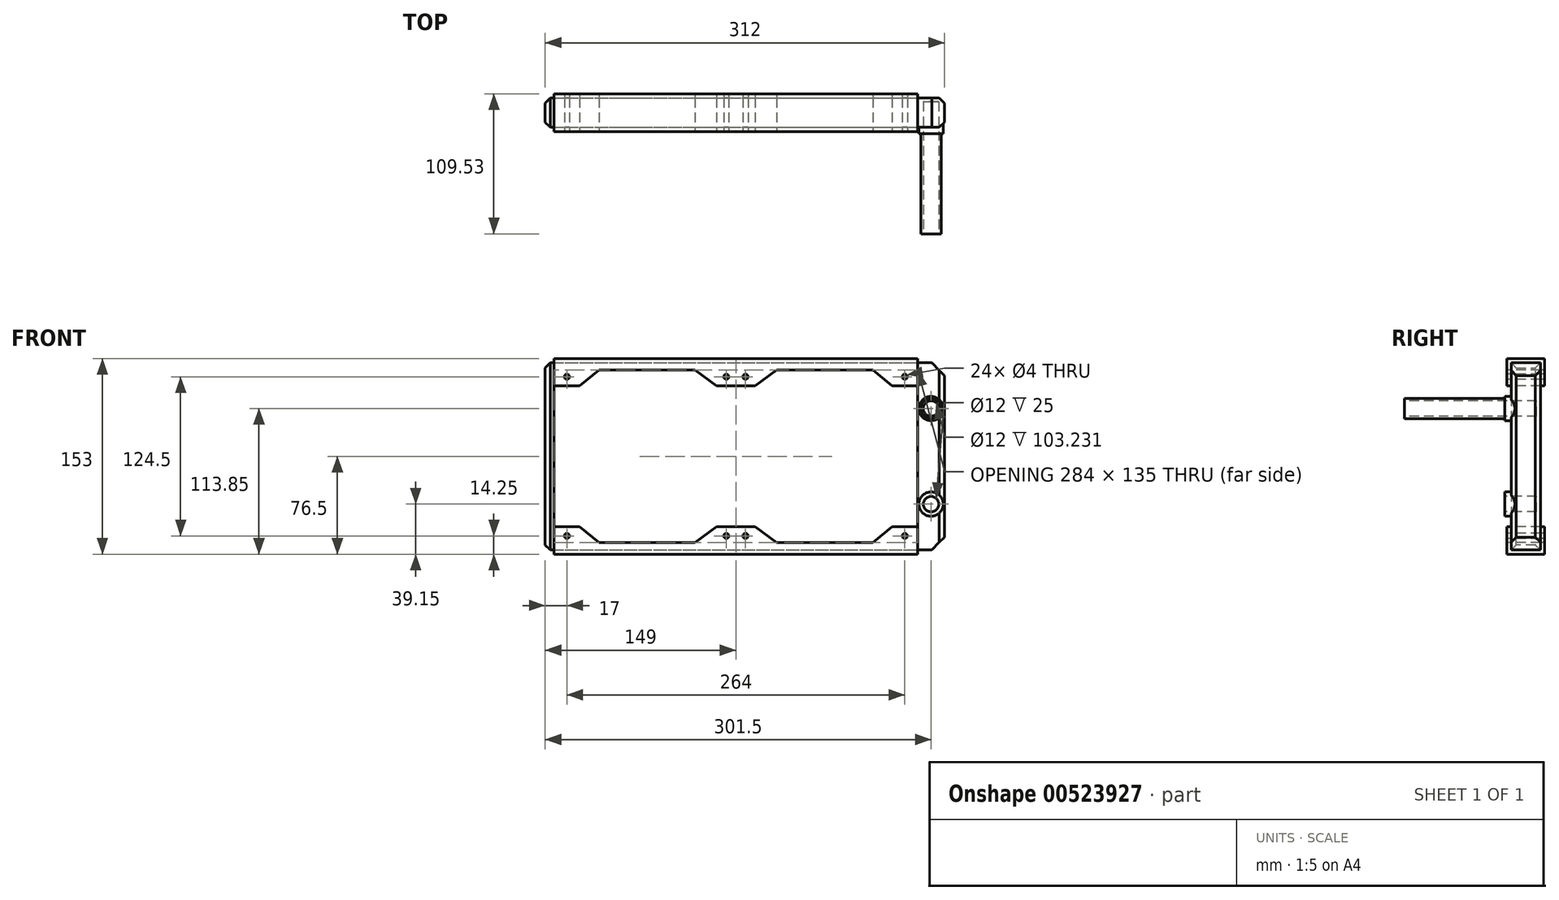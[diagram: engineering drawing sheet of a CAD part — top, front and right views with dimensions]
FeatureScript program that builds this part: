
annotation { "Feature Type Name" : "Feature", "Feature Type Description" : "" }
export const myFeature = defineFeature(function(context is Context, id is Id, definition is map)
    precondition{}
    {
        {
            var Q0;
            Q0=qCreatedBy(makeId("Front.planeOp"),FACE);
            var sketch = newSketch(context, id + "F0", { "sketchPlane" : qUnion([Q0])});
            skLineSegment(sketch, "E0.bottom", {"start": v(0, 73.2) * mm, "end": v(312, 73.2) * mm});
            skLineSegment(sketch, "E0.top", {"start": v(0, -73.2) * mm, "end": v(312, -73.2) * mm});
            skLineSegment(sketch, "E0.left", {"start": v(0, 73.2) * mm, "end": v(0, -73.2) * mm});
            skLineSegment(sketch, "E0.right", {"start": v(312, 73.2) * mm, "end": v(312, -73.2) * mm});
            skPoint(sketch, "E1", {"position": v(0, 0) * mm});
            skSolve(sketch);
        }
        {
            var Q0;
            Q0=qSketchRegion(id+"F0",true);
            extrude(context, id + "F1", {"entities" : qUnion([Q0]), "depth" : 23 * mm});
        }
        {
            var Q0;
            Q0=makeQuery(id+"F1.opExtrude","CAP_FACE",FACE,{"disambiguationData":[OSD([sQuery(id+"F0.wireOp",EDGE,"E0.bottom"),sQuery(id+"F0.wireOp",EDGE,"E0.top"),sQuery(id+"F0.wireOp",EDGE,"E0.left"),sQuery(id+"F0.wireOp",EDGE,"E0.right")])],"isStart":false});
            var sketch = newSketch(context, id + "F2", { "sketchPlane" : qUnion([Q0])});
            skCircle(sketch, "E2", {"center": v(301.5, 37.35) * mm, "radius": 9.5 * mm});
            skCircle(sketch, "E3", {"center": v(301.5, -37.35) * mm, "radius": 9.5 * mm});
            skLineSegment(sketch, "E4", {"start": v(312, 0) * mm, "end": v(0, 0) * mm, "construction": true});
            skSolve(sketch);
        }
        {
            var Q0;
            Q0=qSketchRegion(id+"F2",true);
            extrude(context, id + "F3", {"entities" : qUnion([Q0]), "operationType" : NewBodyOperationType.ADD, "depth" : 5 * mm});
        }
        {
            var Q0;
            Q0=makeQuery(id+"F3.opExtrude","CAP_FACE",FACE,{"disambiguationData":[OSD([sQuery(id+"F2.wireOp",EDGE,"E2")])],"isStart":false});
            var sketch = newSketch(context, id + "F4", { "sketchPlane" : qUnion([Q0])});
            skCircle(sketch, "E5", {"center": v(301.5, 37.35) * mm, "radius": 6 * mm});
            skCircle(sketch, "E6", {"center": v(301.5, -37.35) * mm, "radius": 6 * mm});
            skSolve(sketch);
        }
        {
            var Q0;
            Q0=qSketchRegion(id+"F4",true);
            extrude(context, id + "F5", {"entities" : qUnion([Q0]), "operationType" : NewBodyOperationType.REMOVE, "oppositeDirection" : true, "depth" : 25 * mm});
        }
        {
            var Q0;
            Q0=makeQuery(id+"F1.opExtrude","SWEPT_EDGE",EDGE,{"disambiguationData":[OSD([sQuery(id+"F0.wireOp",EDGE,"E0.top"),sQuery(id+"F0.wireOp",EDGE,"E0.right")])]});
            var Q1;
            Q1=makeQuery(id+"F1.opExtrude","SWEPT_EDGE",EDGE,{"disambiguationData":[OSD([sQuery(id+"F0.wireOp",EDGE,"E0.bottom"),sQuery(id+"F0.wireOp",EDGE,"E0.right")])]});
            chamfer(context, id + "F6", {"entities" : qUnion([Q0, Q1]), "width" : 10 * mm, "tangentPropagation" : true});
        }
        {
            var Q0;
            Q0=makeQuery(id+"F1.opExtrude","CAP_EDGE",EDGE,{"disambiguationData":[OSD([sQuery(id+"F0.wireOp",EDGE,"E0.right")])],"isStart":false});
            var Q1;
            Q1=makeQuery(id+"F1.opExtrude","CAP_EDGE",EDGE,{"disambiguationData":[OSD([sQuery(id+"F0.wireOp",EDGE,"E0.right")])],"isStart":true});
            var Q2;
            Q2=makeQuery(id+"F1.opExtrude","CAP_EDGE",EDGE,{"disambiguationData":[OSD([sQuery(id+"F0.wireOp",EDGE,"E0.left")])],"isStart":false});
            var Q3;
            Q3=makeQuery(id+"F1.opExtrude","CAP_EDGE",EDGE,{"disambiguationData":[OSD([sQuery(id+"F0.wireOp",EDGE,"E0.left")])],"isStart":true});
            var Q4;
            Q4=makeQuery(id+"F1.opExtrude","SWEPT_EDGE",EDGE,{"disambiguationData":[OSD([sQuery(id+"F0.wireOp",EDGE,"E0.top"),sQuery(id+"F0.wireOp",EDGE,"E0.left")])]});
            var Q5;
            Q5=makeQuery(id+"F1.opExtrude","SWEPT_EDGE",EDGE,{"disambiguationData":[OSD([sQuery(id+"F0.wireOp",EDGE,"E0.bottom"),sQuery(id+"F0.wireOp",EDGE,"E0.left")])]});
            chamfer(context, id + "F7", {"entities" : qUnion([Q0, Q1, Q2, Q3, Q4, Q5]), "width" : 4 * mm, "tangentPropagation" : true});
        }
        {
            var Q0;
            Q0=makeQuery(id+"F1.opExtrude","SWEPT_FACE",FACE,{"disambiguationData":[OSD([sQuery(id+"F0.wireOp",EDGE,"E0.left")])]});
            cPlane(context, id + "F8", {"entities" : qUnion([Q0]), "cplaneType" : CPlaneType.OFFSET, "offset" : 7 * mm, "oppositeDirection" : true, "width" : 150 * mm, "height" : 150 * mm});
        }
        {
            var Q0;
            Q0=qCreatedBy(id+"F8.planeOp",FACE);
            var sketch = newSketch(context, id + "F9", { "sketchPlane" : qUnion([Q0])});
            skLineSegment(sketch, "E7.bottom", {"start": v(-3.3, 76.5) * mm, "end": v(26.3, 76.5) * mm});
            skLineSegment(sketch, "E7.top", {"start": v(-3.3, -76.5) * mm, "end": v(26.3, -76.5) * mm});
            skLineSegment(sketch, "E7.left", {"start": v(-3.3, 76.5) * mm, "end": v(-3.3, -76.5) * mm});
            skLineSegment(sketch, "E7.right", {"start": v(26.3, 76.5) * mm, "end": v(26.3, -76.5) * mm});
            skLineSegment(sketch, "E8", {"start": v(0, 0) * mm, "end": v(-3.3, 0) * mm, "construction": true});
            skLineSegment(sketch, "E9.bottom", {"start": v(0, 73.2) * mm, "end": v(23, 73.2) * mm});
            skLineSegment(sketch, "E9.top", {"start": v(0, -73.2) * mm, "end": v(23, -73.2) * mm});
            skLineSegment(sketch, "E9.left", {"start": v(0, 73.2) * mm, "end": v(0, -73.2) * mm});
            skLineSegment(sketch, "E9.right", {"start": v(23, 73.2) * mm, "end": v(23, -73.2) * mm});
            skSolve(sketch);
        }
        {
            var Q0;
            Q0=qSketchRegion(id+"F9",true);
            extrude(context, id + "F10", {"entities" : qUnion([Q0]), "oppositeDirection" : true, "depth" : 284 * mm});
        }
        {
            var Q0;
            Q0=makeQuery(id+"F10.opExtrude","SWEPT_FACE",FACE,{"disambiguationData":[OSD([sQuery(id+"F9.wireOp",EDGE,"E7.right")])]});
            var sketch = newSketch(context, id + "F11", { "sketchPlane" : qUnion([Q0])});
            skCircle(sketch, "E10", {"center": v(17, 62.25) * mm, "radius": 2 * mm});
            skCircle(sketch, "E11", {"center": v(141.5, 62.25) * mm, "radius": 2 * mm});
            skCircle(sketch, "E12", {"center": v(156.5, 62.25) * mm, "radius": 2 * mm});
            skCircle(sketch, "E13", {"center": v(281, 62.25) * mm, "radius": 2 * mm});
            skLineSegment(sketch, "E14", {"start": v(7, 0) * mm, "end": v(291, 0) * mm, "construction": true});
            skLineSegment(sketch, "E15", {"start": v(149, 76.5) * mm, "end": v(149, -76.5) * mm, "construction": true});
            skCircle(sketch, "E16.MirrorC", {"center": v(17, -62.25) * mm, "radius": 2 * mm});
            skCircle(sketch, "E17.MirrorC", {"center": v(141.5, -62.25) * mm, "radius": 2 * mm});
            skCircle(sketch, "E18.MirrorC", {"center": v(156.5, -62.25) * mm, "radius": 2 * mm});
            skCircle(sketch, "E19.MirrorC", {"center": v(281, -62.25) * mm, "radius": 2 * mm});
            skSolve(sketch);
        }
        {
            var Q0;
            Q0=qSketchRegion(id+"F11",true);
            extrude(context, id + "F12", {"entities" : qUnion([Q0]), "operationType" : NewBodyOperationType.REMOVE, "endBound" : BoundingType.THROUGH_ALL, "oppositeDirection" : true, "depth" : 25 * mm});
        }
        {
            var Q0;
            Q0=makeQuery(id+"F10.opExtrude","SWEPT_FACE",FACE,{"disambiguationData":[OSD([sQuery(id+"F9.wireOp",EDGE,"E7.right")])]});
            var sketch = newSketch(context, id + "F13", { "sketchPlane" : qUnion([Q0])});
            skLineSegment(sketch, "E20", {"start": v(7, 55) * mm, "end": v(27, 55) * mm});
            skLineSegment(sketch, "E21", {"start": v(27, 55) * mm, "end": v(42, 67.5) * mm});
            skLineSegment(sketch, "E22", {"start": v(42, 67.5) * mm, "end": v(117, 67.5) * mm});
            skLineSegment(sketch, "E23", {"start": v(117, 67.5) * mm, "end": v(134, 55) * mm});
            skLineSegment(sketch, "E24", {"start": v(134, 55) * mm, "end": v(164, 55) * mm});
            skLineSegment(sketch, "E25", {"start": v(164, 55) * mm, "end": v(181, 67.5) * mm});
            skLineSegment(sketch, "E26", {"start": v(181, 67.5) * mm, "end": v(256, 67.5) * mm});
            skLineSegment(sketch, "E27", {"start": v(256, 67.5) * mm, "end": v(271, 55) * mm});
            skLineSegment(sketch, "E28", {"start": v(271, 55) * mm, "end": v(291, 55) * mm});
            skLineSegment(sketch, "E29", {"start": v(291, 55) * mm, "end": v(291, 0) * mm});
            skLineSegment(sketch, "E30", {"start": v(7, 55) * mm, "end": v(7, 0) * mm});
            skLineSegment(sketch, "E31", {"start": v(7, 0) * mm, "end": v(291, 0) * mm, "construction": true});
            skLineSegment(sketch, "E32", {"start": v(149, 76.5) * mm, "end": v(149, 55) * mm, "construction": true});
            skLineSegment(sketch, "E33.MirrorCS", {"start": v(291, -55) * mm, "end": v(291, 0) * mm});
            skLineSegment(sketch, "E34.MirrorCS", {"start": v(271, -55) * mm, "end": v(291, -55) * mm});
            skLineSegment(sketch, "E35.MirrorCS", {"start": v(256, -67.5) * mm, "end": v(271, -55) * mm});
            skLineSegment(sketch, "E36.MirrorCS", {"start": v(181, -67.5) * mm, "end": v(256, -67.5) * mm});
            skLineSegment(sketch, "E37.MirrorCS", {"start": v(164, -55) * mm, "end": v(181, -67.5) * mm});
            skLineSegment(sketch, "E38.MirrorCS", {"start": v(134, -55) * mm, "end": v(164, -55) * mm});
            skLineSegment(sketch, "E39.MirrorCS", {"start": v(117, -67.5) * mm, "end": v(134, -55) * mm});
            skLineSegment(sketch, "E40.MirrorCS", {"start": v(42, -67.5) * mm, "end": v(117, -67.5) * mm});
            skLineSegment(sketch, "E41.MirrorCS", {"start": v(27, -55) * mm, "end": v(42, -67.5) * mm});
            skLineSegment(sketch, "E42.MirrorCS", {"start": v(7, -55) * mm, "end": v(7, 0) * mm});
            skLineSegment(sketch, "E43.MirrorCS", {"start": v(7, -55) * mm, "end": v(27, -55) * mm});
            skSolve(sketch);
        }
        {
            var Q0;
            Q0=qSketchRegion(id+"F13",true);
            extrude(context, id + "F14", {"entities" : qUnion([Q0]), "operationType" : NewBodyOperationType.REMOVE, "endBound" : BoundingType.THROUGH_ALL, "oppositeDirection" : true, "depth" : 25 * mm});
        }
        {
            var Q0;
            Q0=makeQuery(id+"F3.opExtrude","CAP_FACE",FACE,{"disambiguationData":[OSD([sQuery(id+"F2.wireOp",EDGE,"E2")])],"isStart":false});
            var sketch = newSketch(context, id + "F15", { "sketchPlane" : qUnion([Q0])});
            skCircle(sketch, "E44", {"center": v(301.5, 37.35) * mm, "radius": 8 * mm});
            skCircle(sketch, "E45", {"center": v(301.5, 37.35) * mm, "radius": 6 * mm});
            skSolve(sketch);
        }
        {
            var Q0;
            Q0=qSketchRegion(id+"F15",true);
            extrude(context, id + "F16", {"entities" : qUnion([Q0]), "operationType" : NewBodyOperationType.ADD, "depth" : 78.23 * mm});
        }
    });
